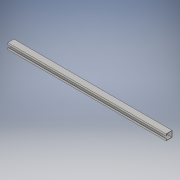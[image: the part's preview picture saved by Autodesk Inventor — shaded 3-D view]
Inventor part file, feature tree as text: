
AUTODESK INVENTOR PART (.ipt)
format: ipt  version: 2016 (Build 200138000, 138)  size: 111,104 bytes
history: native  units: mm
features: extrude x2, sketch x2
ambient origin geometry x8: Origin, YZ Plane, XZ Plane, XY Plane, X Axis, Y Axis, Z Axis, Center Point
bodies: Solid1 (feature_tree)
feature tree (4):
  extrude  "Extrusion1"  Depth=50.0mm
  extrude  "Extrusion2"  Depth=20.0mm
  sketch  "Sketch1"  dims[d0=50.0mm d1=50.0mm]
  sketch  "Sketch2"  dims[d2=10.0mm d3=20.0mm d4=1300.0mm d5=0.0mm d6=3.0mm d7=3.0mm d8=3.0mm d9=3.0mm d10=1300.0mm d11=0.0mm]
